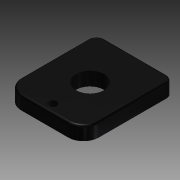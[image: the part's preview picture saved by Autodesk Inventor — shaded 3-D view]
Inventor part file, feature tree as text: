
AUTODESK INVENTOR PART (.ipt)
format: ipt  version: 2015 (Build 190159000, 159)  size: 113,152 bytes
history: native  units: in
note: dims shown in document units (in); Inventor stores cm internally (conversion verified against a paired STEP export)
features: extrude x1, fillet x1, sketch x1
ambient origin geometry x8: Origin, YZ Plane, XZ Plane, XY Plane, X Axis, Y Axis, Z Axis, Center Point
bodies: Solid1 (feature_tree)
feature tree (3):
  extrude  "Extrusion1"  Depth=6.0in
  fillet  "Fillet1"  Radius=1.1811in
  sketch  "Sketch1"  dims[d0=7.0in d1=6.0in d2=1.1811in d3=0.5906in d4=0.625in d5=0.625in d6=1.0531in d7=0.0in d8=0.1575in d9=2.1654in]
